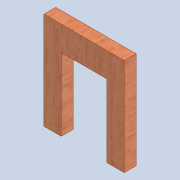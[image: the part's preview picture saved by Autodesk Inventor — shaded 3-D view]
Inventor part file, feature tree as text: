
AUTODESK INVENTOR PART (.ipt)
format: ipt  version: 2020 (Build 240168000, 168)  size: 217,088 bytes
history: native  units: mm
features: reference x4, other x3, extrude x2, sketch x2
ambient origin geometry x8: Origin, YZ Plane, XZ Plane, XY Plane, X Axis, Y Axis, Z Axis, Center Point
bodies: Solid1 (feature_tree)
feature tree (11):
  extrude  "Extrusion1"  Depth=66.0mm
  extrude  "Extrusion2"  TaperAngle=0.0deg  [1 undecoded]
  sketch  "Sketch1"  dims[d0=54.5mm d1=66.0mm]
  sketch  "Sketch2"  dims[d2=8.0mm d3=0.0mm d6=0.0mm d7=0.0mm d29=2.0mm d30=2.0mm d32=2.0mm]
  reference  "Reference8"
  reference  "Reference9"
  reference  "Reference10"
  reference  "Reference11"
  parser-record x1  (decoder bookkeeping rows leaked as tree rows — omitted from the tree; the rows remain in map.json)
  other  "0005-00-00 Ansamblu_General.iam"
  other  "Inlet Module Plug Fuse Switch Male Power Socket 10A 250V 3 Pin IEC320 C14:1"
note: 1 required parameter value undecoded (feature->parameter linkage not recoverable at this tier; creation-order binding heuristic only, values carry confidence <= 0.55)
note: 1 file-system path scrubbed to <path> (originals preserved in map.json)
